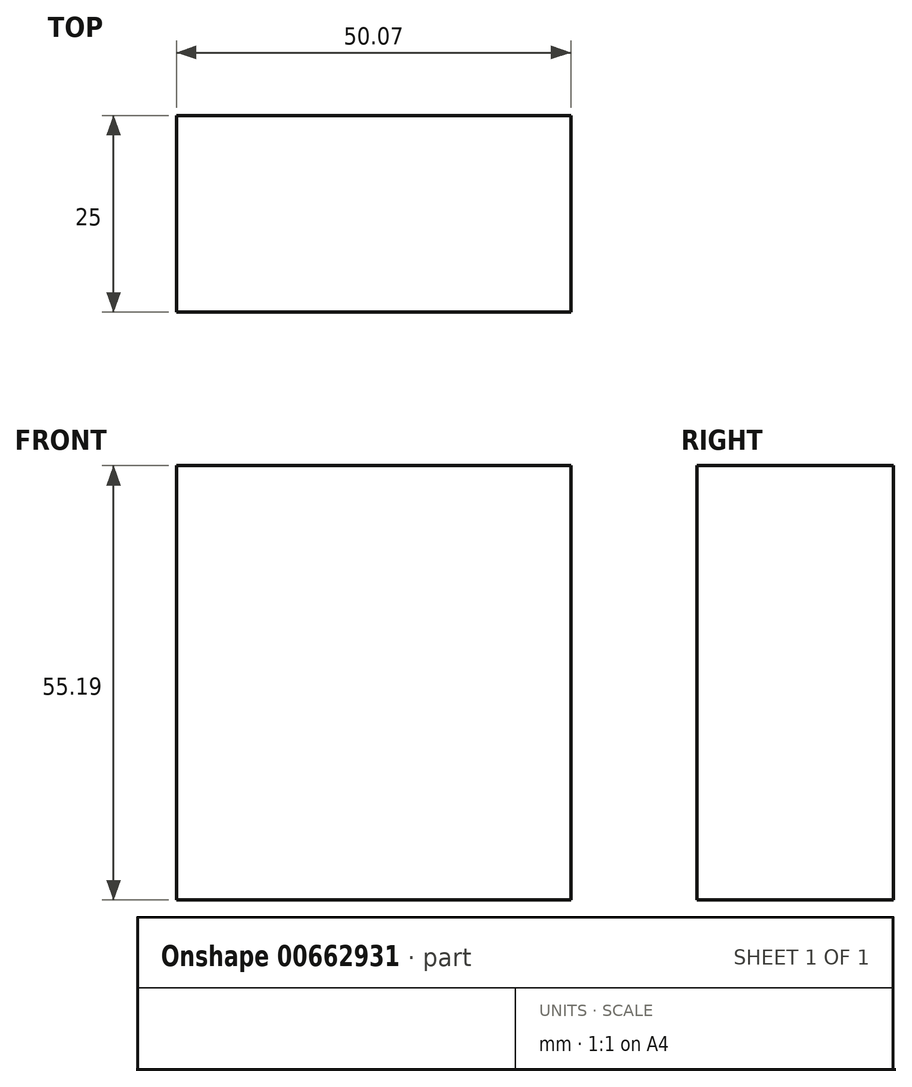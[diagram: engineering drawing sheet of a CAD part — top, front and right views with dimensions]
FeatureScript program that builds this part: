
annotation { "Feature Type Name" : "Feature", "Feature Type Description" : "" }
export const myFeature = defineFeature(function(context is Context, id is Id, definition is map)
    precondition{}
    {
        {
            var Q0;
            Q0=qCreatedBy(makeId("Front.planeOp"),FACE);
            var sketch = newSketch(context, id + "F0", { "sketchPlane" : qUnion([Q0])});
            skLineSegment(sketch, "E0.bottom", {"start": v(-102.3, 0) * mm, "end": v(-52.24, 0) * mm});
            skLineSegment(sketch, "E0.top", {"start": v(-102.3, 55.19) * mm, "end": v(-52.24, 55.19) * mm});
            skLineSegment(sketch, "E0.left", {"start": v(-102.3, 0) * mm, "end": v(-102.3, 55.19) * mm});
            skLineSegment(sketch, "E0.right", {"start": v(-52.24, 0) * mm, "end": v(-52.24, 55.19) * mm});
            skPoint(sketch, "E0.middle", {"position": v(-77.27, 27.6) * mm});
            skSolve(sketch);
        }
        {
            var Q0;
            Q0=makeQuery(id+"F0.imprint","IMPRINT",FACE,{"disambiguationData":[TD([[makeQuery(id+"F0.imprint","IMPRINT",EDGE,{"derivedFrom":sQuery(id+"F0.wireOp",EDGE,"E0.bottom")}),1.0]])]});
            extrude(context, id + "F1", {"entities" : qUnion([Q0]), "depth" : 25 * mm, "offsetDistance" : 25 * mm});
        }
    });
